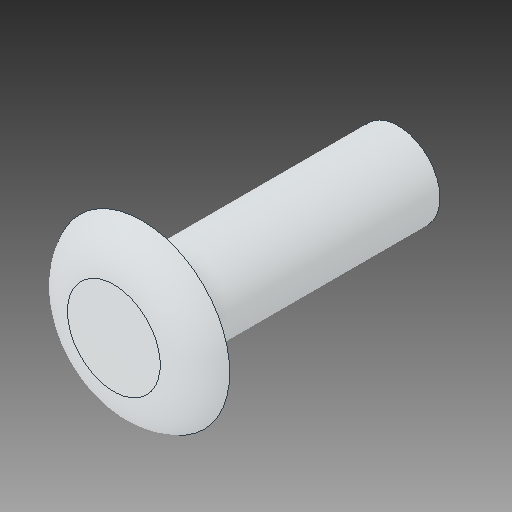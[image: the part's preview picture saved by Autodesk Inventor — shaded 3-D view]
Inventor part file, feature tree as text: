
AUTODESK INVENTOR PART (.ipt)
format: ipt  version: 2018 (Build 220112000, 112)  size: 111,616 bytes
history: native  units: in
note: dims shown in document units (in); Inventor stores cm internally (conversion verified against a paired STEP export)
features: fillet x1
ambient origin geometry x8: Origin, YZ Plane, XZ Plane, XY Plane, X Axis, Y Axis, Z Axis, Center Point
bodies: Solid1 (feature_tree)
feature tree (1):
  fillet  "Fillet1"  [1 undecoded]
note: 1 required parameter value undecoded (feature->parameter linkage not recoverable at this tier; creation-order binding heuristic only, values carry confidence <= 0.55)
